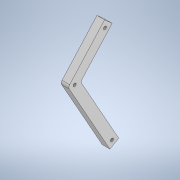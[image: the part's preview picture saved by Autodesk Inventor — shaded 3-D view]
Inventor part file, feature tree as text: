
AUTODESK INVENTOR PART (.ipt)
format: ipt  version: 2020 (Build 240168000, 168)  size: 142,336 bytes
history: native  units: in
note: dims shown in document units (in); Inventor stores cm internally (conversion verified against a paired STEP export)
features: extrude x2, sketch x2
ambient origin geometry x8: Origin, YZ Plane, XZ Plane, XY Plane, X Axis, Y Axis, Z Axis, Center Point
bodies: Solid1 (feature_tree)
feature tree (4):
  extrude  "Extrusion1"  Depth=0.5906in TaperAngle=0.0deg
  extrude  "Extrusion2"  Depth=0.3937in
  sketch  "Sketch1"  dims[d0=0.7874in d1=6.2992in d2=0.7874in d3=0.3937in d4=0.7874in d5=3.937in d6=0.3937in d7=0.7874in d8=0.2362in d9=0.2362in d10=0.2362in d11=0.2362in d12=0.5906in d13=0.0in]
  sketch  "Sketch2"  dims[d14=0.2756in d15=0.2756in d16=0.3937in d17=0.3937in d18=0.2362in d19=0.2362in d20=0.3937in d21=0.3937in d22=0.2362in d23=0.3937in d24=0.3937in d25=0.0in d26=0.0in d27=0.7463in]
